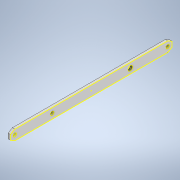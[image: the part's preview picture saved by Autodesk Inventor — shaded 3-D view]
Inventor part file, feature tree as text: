
AUTODESK INVENTOR PART (.ipt)
format: ipt  version: 2020 (Build 240168000, 168)  size: 223,744 bytes
history: native  units: in
note: dims shown in document units (in); Inventor stores cm internally (conversion verified against a paired STEP export)
features: sketch x6, extrude x5, projected_geometry x4, other x3
ambient origin geometry x8: Origin, YZ Plane, XZ Plane, XY Plane, X Axis, Y Axis, Z Axis, Center Point
bodies: Solid1 (feature_tree)
feature tree (18):
  other  "HexWheelGuard.ipt"
  extrude  "Extrusion1"  TaperAngle=0.0deg  [1 undecoded]
  extrude  "Extrusion2"  Depth=0.3937in
  extrude  "Extrusion3"  Depth=0.3937in TaperAngle=0.0deg
  extrude  "Extrusion4"  Depth=0.3543in
  extrude  "Extrusion5"  Depth=0.0787in
  sketch  "Sketch6"  dims[d17=1.5748in d18=0.5906in]
  other  "Solid1::HexWheelGuard.ipt"
  other  "TaggingFeature1"
  sketch  "Sketch1"  dims[d0=0.3937in d1=0.0in d2=0.0in]
  projected_geometry  "Projected Loop1"
  sketch  "Sketch2"  dims[d3=0.3937in d4=0.0in d5=0.122in]
  sketch  "Sketch3"  dims[d6=0.122in d7=0.3937in d8=0.0in]
  sketch  "Sketch4"  dims[d10=0.3937in d11=0.0in d12=0.3543in]
  projected_geometry  "Projected Loop2"
  sketch  "Sketch5"  dims[d13=0.0787in d14=0.0in d15=0.122in]
  projected_geometry  "Projected Loop3"
  projected_geometry  "Projected Loop4"
note: 1 required parameter value undecoded (feature->parameter linkage not recoverable at this tier; creation-order binding heuristic only, values carry confidence <= 0.55)
